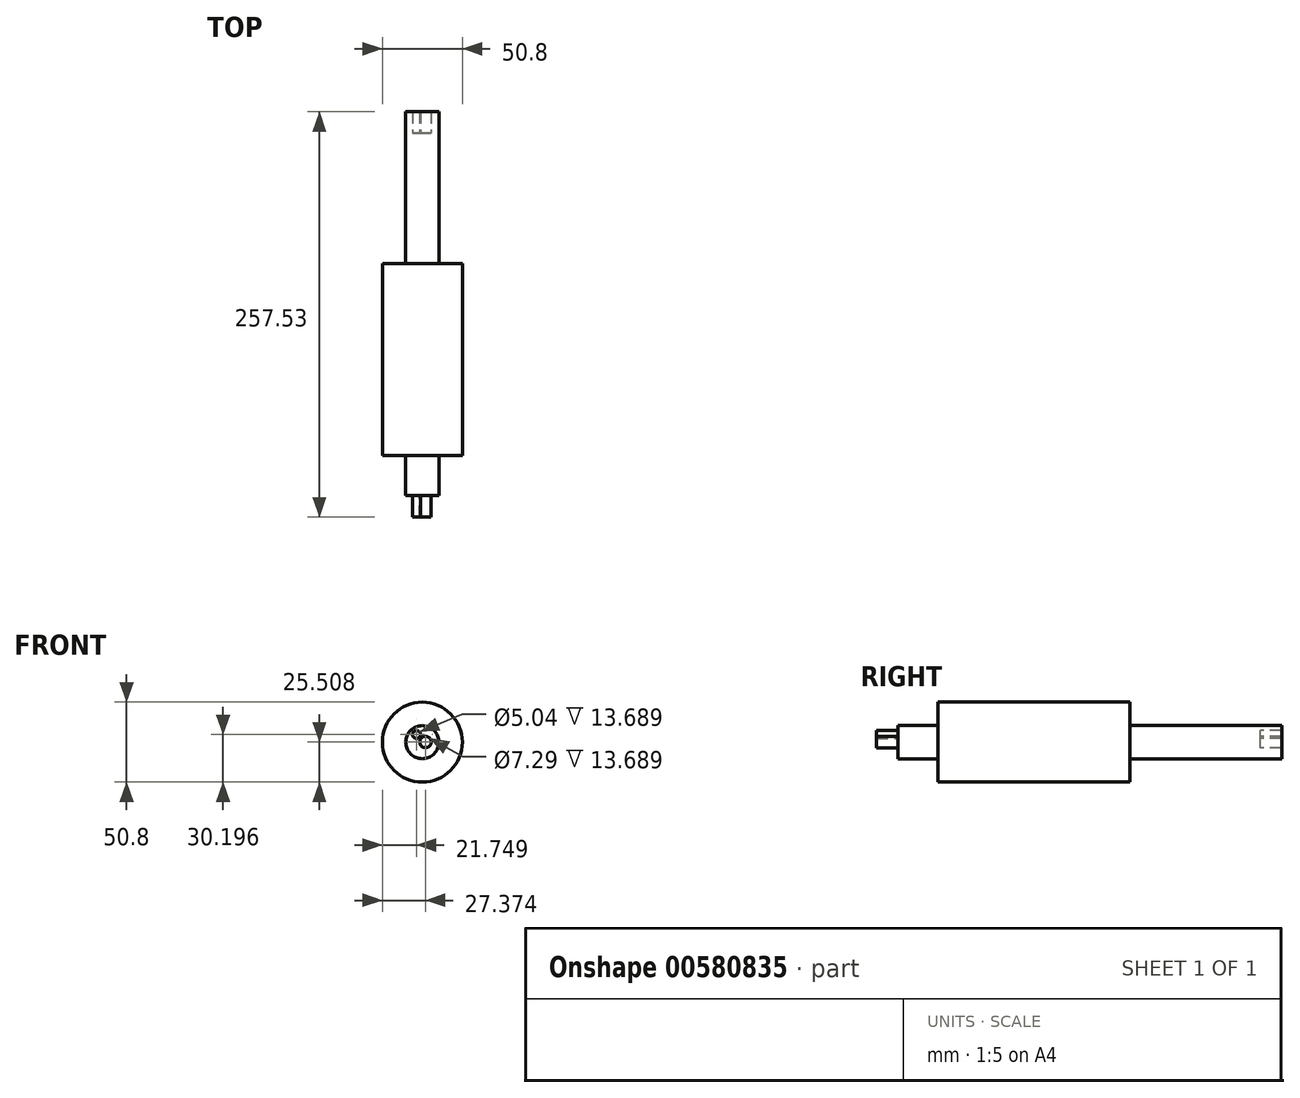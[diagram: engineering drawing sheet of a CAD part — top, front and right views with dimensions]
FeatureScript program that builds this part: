
annotation { "Feature Type Name" : "Feature", "Feature Type Description" : "" }
export const myFeature = defineFeature(function(context is Context, id is Id, definition is map)
    precondition{}
    {
        {
            var Q0;
            Q0=qCreatedBy(makeId("Front.planeOp"),FACE);
            var sketch = newSketch(context, id + "F0", { "sketchPlane" : qUnion([Q0])});
            skCircle(sketch, "E0", {"center": v(9.31, 20.82) * mm, "radius": 10.5 * mm});
            skSolve(sketch);
        }
        {
            var Q0;
            Q0 = qSketchRegion(id + "F0", true);
            extrude(context, id + "F1", {"entities" : qUnion([Q0]), "depth" : 25.4 * mm, "offsetDistance" : 25.4 * mm});
        }
        {
            var Q0;
            Q0=qCreatedBy(makeId("Front.planeOp"),FACE);
            var sketch = newSketch(context, id + "F2", { "sketchPlane" : qUnion([Q0])});
            skCircle(sketch, "E1", {"center": v(5.66, 25.62) * mm, "radius": 2.52 * mm});
            skCircle(sketch, "E2", {"center": v(11.28, 20.93) * mm, "radius": 3.64 * mm});
            skSolve(sketch);
        }
        {
            var Q0;
            Q0 = qSketchRegion(id + "F2", true);
            extrude(context, id + "F3", {"entities" : qUnion([Q0]), "operationType" : NewBodyOperationType.ADD, "endBound" : BoundingType.THROUGH_ALL, "depth" : 25.4 * mm, "offsetDistance" : 25.4 * mm});
        }
        {
            var Q0;
            Q0=makeQuery(id+"F1.opExtrude","CAP_FACE",FACE,{"disambiguationData":[OSD([sQuery(id+"F0.wireOp",EDGE,"E0")])],"isStart":true});
            var sketch = newSketch(context, id + "F4", { "sketchPlane" : qUnion([Q0])});
            skCircle(sketch, "E3", {"center": v(-9.31, 20.82) * mm, "radius": 25.4 * mm});
            skSolve(sketch);
        }
        {
            var Q0;
            Q0=makeQuery(id+"F4.imprint","IMPRINT",FACE,{"disambiguationData":[TD([[makeQuery(id+"F4.imprint","IMPRINT",EDGE,{"derivedFrom":makeQuery(id+"F1.opExtrude","CAP_EDGE",EDGE,{"disambiguationData":[OSD([sQuery(id+"F0.wireOp",EDGE,"E0")])],"isStart":true})}),-1.0]])]});
            var Q1;
            Q1=makeQuery(id+"F4.imprint","IMPRINT",FACE,{"disambiguationData":[TD([[makeQuery(id+"F4.imprint","IMPRINT",EDGE,{"derivedFrom":sQuery(id+"F4.wireOp",EDGE,"E3")}),1.0]])]});
            extrude(context, id + "F5", {"entities" : qUnion([Q0, Q1]), "operationType" : NewBodyOperationType.ADD, "depth" : 25.4 * mm, "offsetDistance" : 25.4 * mm});
        }
        {
            var Q0;
            Q0=makeQuery(id+"F5.opExtrude","CAP_FACE",FACE,{"disambiguationData":[OSD([sQuery(id+"F4.wireOp",EDGE,"E3")])],"isStart":false});
            extrude(context, id + "F6", {"entities" : qUnion([Q0]), "operationType" : NewBodyOperationType.ADD, "endBound" : BoundingType.THROUGH_ALL, "depth" : 25.4 * mm, "offsetDistance" : 25.4 * mm});
        }
        {
            var Q0;
            Q0=makeQuery(id+"F3.opExtrude","CAP_FACE",FACE,{"disambiguationData":[OSD([sQuery(id+"F2.wireOp",EDGE,"E1")])],"isStart":false});
            var Q1;
            Q1=makeQuery(id+"F3.opExtrude","CAP_FACE",FACE,{"disambiguationData":[OSD([sQuery(id+"F2.wireOp",EDGE,"E2")])],"isStart":false});
            var Q2;
            Q2=makeQuery(id+"F1.opExtrude","CAP_FACE",FACE,{"disambiguationData":[OSD([sQuery(id+"F0.wireOp",EDGE,"E0")])],"isStart":false});
            extrude(context, id + "F7", {"entities" : qUnion([Q0, Q1, Q2]), "operationType" : NewBodyOperationType.ADD, "oppositeDirection" : true, "depth" : 243.84 * mm, "offsetDistance" : 25.4 * mm});
        }
    });
